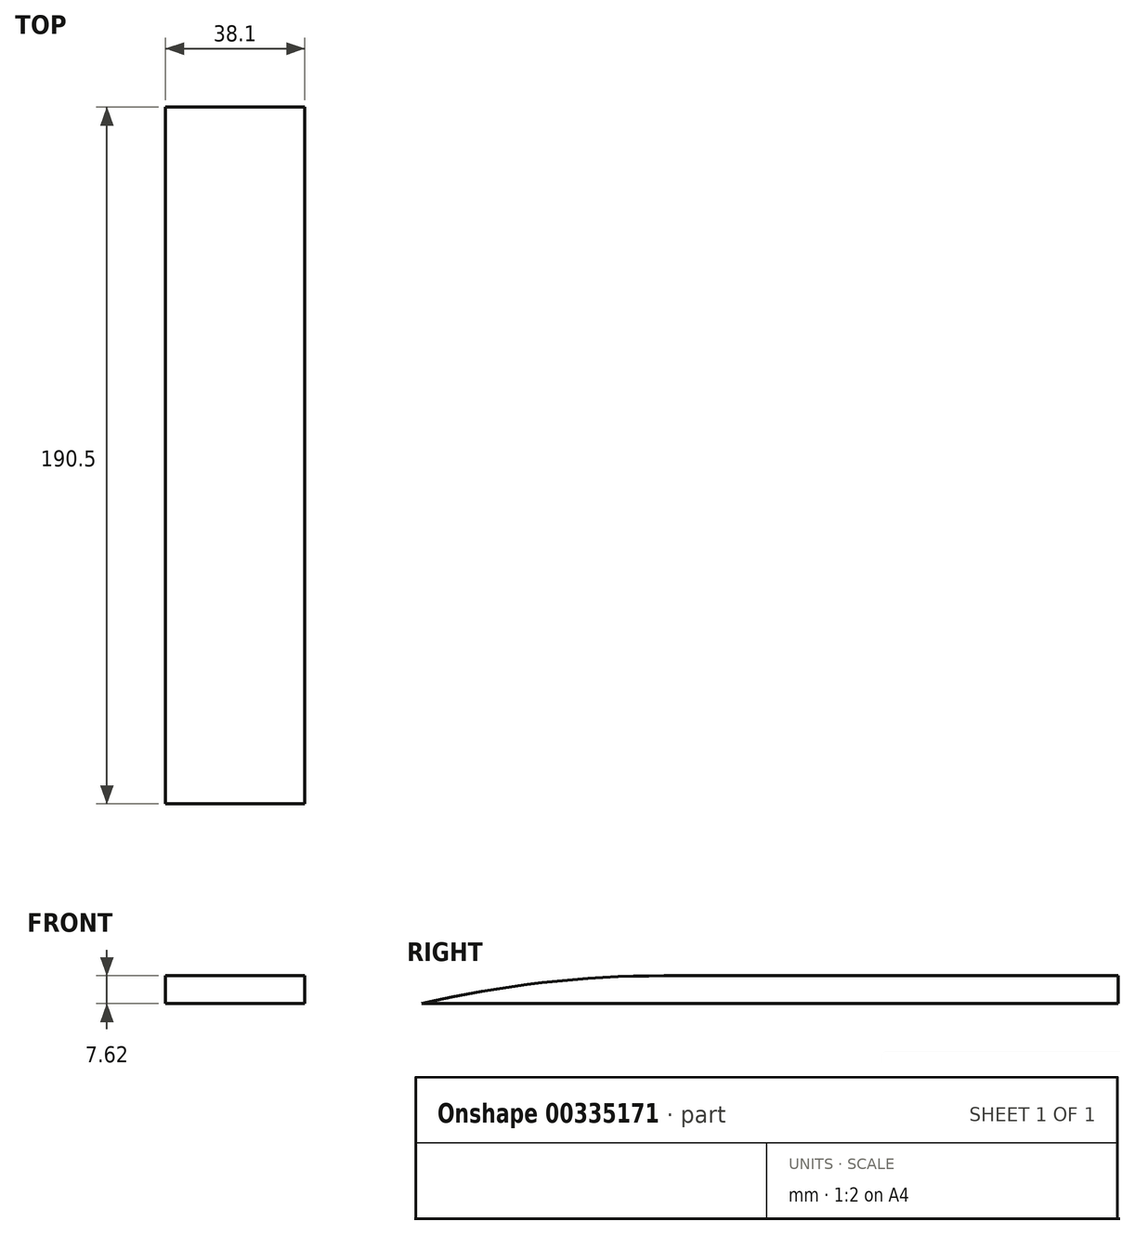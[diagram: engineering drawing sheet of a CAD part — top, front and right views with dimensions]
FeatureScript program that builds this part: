
annotation { "Feature Type Name" : "Feature", "Feature Type Description" : "" }
export const myFeature = defineFeature(function(context is Context, id is Id, definition is map)
    precondition{}
    {
        {
            var Q0;
            Q0=qCreatedBy(makeId("Top.planeOp"),FACE);
            var sketch = newSketch(context, id + "F0", { "sketchPlane" : qUnion([Q0])});
            skLineSegment(sketch, "E0", {"start": v(-26.5, 0) * mm, "end": v(11.6, 0) * mm});
            skLineSegment(sketch, "E1", {"start": v(-26.5, 0) * mm, "end": v(-26.5, -190.5) * mm});
            skLineSegment(sketch, "E2", {"start": v(11.6, 0) * mm, "end": v(11.6, -190.5) * mm});
            skLineSegment(sketch, "E3", {"start": v(11.6, -190.5) * mm, "end": v(-26.5, -190.5) * mm});
            skSolve(sketch);
        }
        {
            var Q0;
            Q0=makeQuery(id+"F0.imprint","IMPRINT",FACE,{"disambiguationData":[TD([[makeQuery(id+"F0.imprint","IMPRINT",EDGE,{"derivedFrom":sQuery(id+"F0.wireOp",EDGE,"E0")}),-1.0]])]});
            extrude(context, id + "F1", {"entities" : qUnion([Q0]), "depth" : 7.62 * mm});
        }
        {
            var Q0;
            Q0=makeQuery(id+"F1.opExtrude","CAP_EDGE",EDGE,{"disambiguationData":[OSD([sQuery(id+"F0.wireOp",EDGE,"E3")])],"isStart":false});
            fillet(context, id + "F2", {"entities" : qUnion([Q0]), "radius" : 291.9 * mm, "tangentPropagation" : true, "allowEdgeOverflow" : false});
        }
    });
